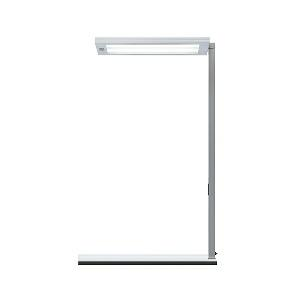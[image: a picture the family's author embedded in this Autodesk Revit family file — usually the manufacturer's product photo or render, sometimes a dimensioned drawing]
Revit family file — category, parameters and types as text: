
# Revit family: lavigo_-_dpt_9000_840_r_g2_00804493_4809
name_source: partatom
category: Lighting Fixtures
units: mm (PartAtom-declared; Revit-internal decimal feet)

## family parameters
Cut with Voids When Loaded = No
Host = Face
Light Source = No
Part Type = Normal
Room Calculation Point = No
Round Connector Dimension = Use Diameter
Shared = No

## types (1)
- LAVIGO - DPT 9000/840/R/G2 (1 x LED, 8950 lm, 4000K)
    Apparent Load = 63 VA
    Approval mark = CE
    CIE Flux Codes = 60 87 97 20 100
    Color Rendering = 80-89
    Color Temperature = 4000K
    Control Gear = Electronic ballast
    Default Elevation = 1800 mm
    Description = DPT 9000/840/R/G2|Desk-mounted luminaire|light source: LED|work equipment: Electronic ballast|connected load: 220-240 V, 50/60 Hz|Power consumption: approx. 63 W|standby: approx. 0,50|power factor: approx. 0,910|luminous flux: 8950 lm|luminous efficacy: 142 lm/W|light distribution: Direct/indirect|direct ratio: approx. 20 %|colour temperature: Cold white, ca. 4000 K|color rendering index (CRI): >= 80|chromaticity tolerance:  3 SDCM|technology: Presence and daylight sensor control (PIR)|operation: Multi-function switch|luminaire body|material: Steel/plastic|surface: Painted|colour: Silver metallic|lamp cover: Acrylic (PMMA), Satine|tubular section|material: Steel tube|surface: Painted|Form: Tubular section upright|colour of tubular section: Silver metallic|weight (net): approx. 9.5 kg|mains lead: 3.70 m Mains plug CEE 7/VII|Fastening: Socket, Table adaptor|decorative contrast side parts: Flint grey|glare control: Prism aperture|luminance(L65): <= 3000 cd/m|unified glare rating(4H 8H): <=  16|special features: Luminaire head detachable, Cradle to Cradle Certified TM, Direct light component with edge light and light-guide technology for homogenous light exit, Flicker-free, Integrated light and presence sensor PIR, Retrofittable with TALK module, Inclination of tubular section adjustable, Separated, direct and indirect light individually adjustable|
    Frequency = 50 Hz, 60 Hz
    Height = 36 mm
    Lamp = 1 x LED
    Lamp Light Flux = 8950 lm
    Lamp count = 1
    Length = 675 mm
    Luminous efficacy = 142 lm/W
    Manufacturer = Waldmann
    ModVariant = No
    Model = 00804493
    Mounting Place = Table
    Mounting Type = Surface mounted
    Number of Poles = 1
    OnlyDefault = Yes
    Power Factor = 1
    Product Name = LAVIGO - DPT 9000/840/R/G2
    Product group = Desk mounted luminaire with detector
    ProductGroupID = 2201
    Protection Class = Protection class I
    Protection Degree = IP 20
    RLX_Detail_Level = 1
    RLX_Emergency_Light_Flux = 0 lm
    RLX_Emergency_Type = 0
    RLX_Emergency_Type_DB = No
    RlxData = <blob elided: 35797 chars, md5=cddc4be7>
    Socket = socket
    Standby Power = 0 W
    System Light Flux = 8950 lm
    System Power = 63 W
    Type Comments = Product without accessories
    Type Image = 121716000-00666945.jpg
    URL = http://relux.com
    VarID = ---
    Voltage = 230 V
    Voltage Range = 220-240 V
    Weight = 0.00 kg
    Width = 320 mm

## geometry (parser evidence)
native form markers: Blend x4, Sweep x14
no freeform markers — native parametric forms only
